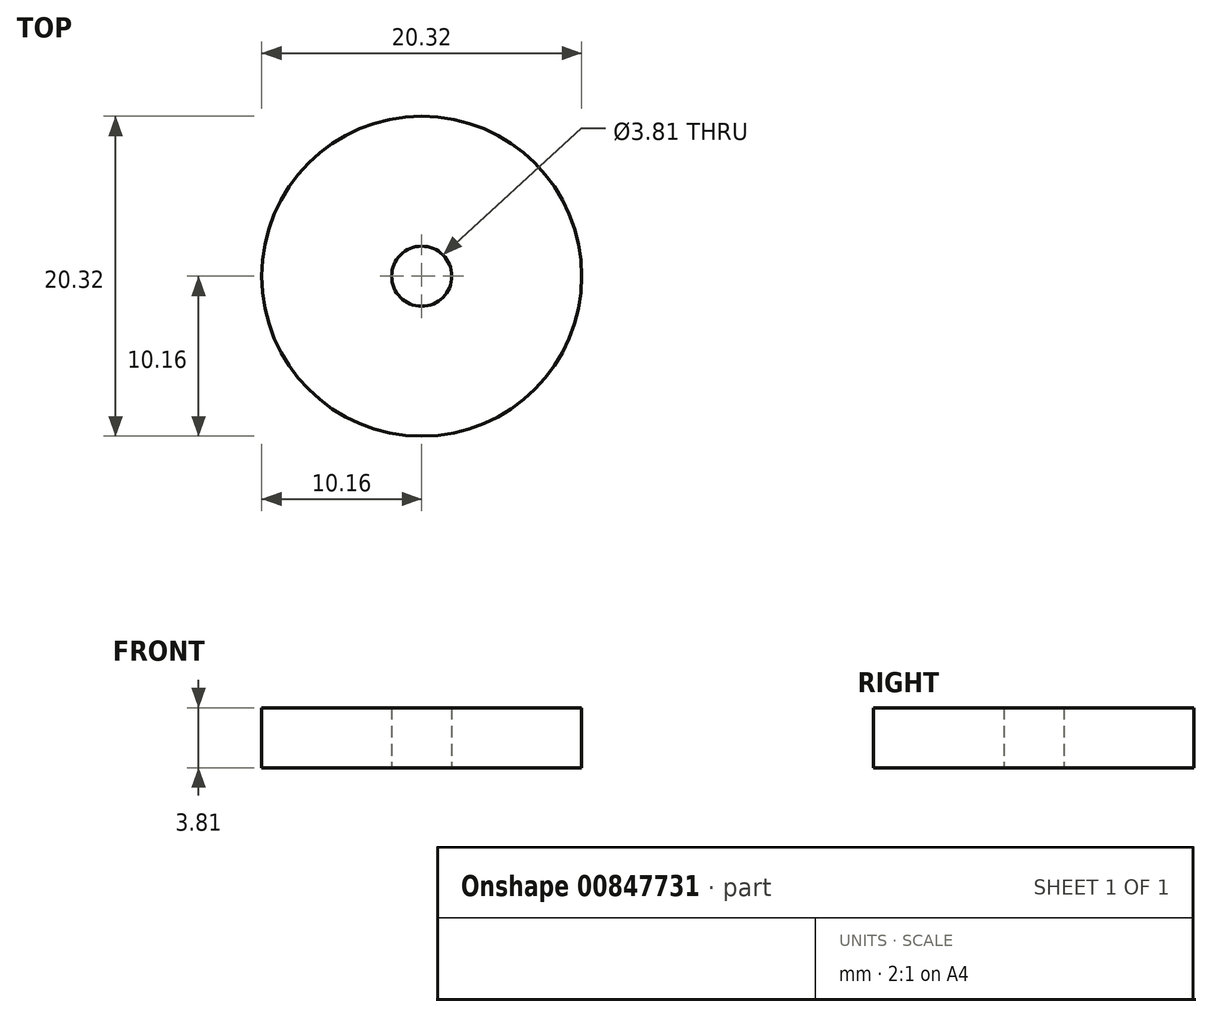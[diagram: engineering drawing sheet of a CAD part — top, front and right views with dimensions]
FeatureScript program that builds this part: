
annotation { "Feature Type Name" : "Feature", "Feature Type Description" : "" }
export const myFeature = defineFeature(function(context is Context, id is Id, definition is map)
    precondition{}
    {
        {
            var Q0;
            Q0=qCreatedBy(makeId("Top.planeOp"),FACE);
            var sketch = newSketch(context, id + "F0", { "sketchPlane" : qUnion([Q0])});
            skCircle(sketch, "E0", {"center": v(0, 0) * mm, "radius": 10.16 * mm});
            skSolve(sketch);
        }
        {
            var Q0;
            Q0=makeQuery(id+"F0.imprint","IMPRINT",FACE,{"disambiguationData":[TD([[makeQuery(id+"F0.imprint","IMPRINT",EDGE,{"derivedFrom":sQuery(id+"F0.wireOp",EDGE,"E0")}),1.0]])]});
            extrude(context, id + "F1", {"entities" : qUnion([Q0]), "depth" : 3.8 * mm, "offsetDistance" : 25.4 * mm});
        }
        {
            var Q0;
            Q0=qCreatedBy(makeId("Front.planeOp"),FACE);
            var sketch = newSketch(context, id + "F2", { "sketchPlane" : qUnion([Q0])});
            skLineSegment(sketch, "E1", {"start": v(-8.9, 3.81) * mm, "end": v(0, 3.81) * mm});
            skLineSegment(sketch, "E2", {"start": v(0, 3.81) * mm, "end": v(0, 1.78) * mm});
            skArc(sketch, "E3", {"start": v(-8.9, 3.8) * mm, "mid": v(-4.56, 2.3) * mm, "end": v(0, 1.78) * mm});
            skLineSegment(sketch, "E4", {"start": v(0, 1.78) * mm, "end": v(21.03, 1.78) * mm, "construction": true});
            skSolve(sketch);
        }
        {
            var Q0;
            Q0=makeQuery(id+"F1.opExtrude","CAP_FACE",FACE,{"disambiguationData":[OSD([sQuery(id+"F0.wireOp",EDGE,"E0")])],"isStart":true});
            var sketch = newSketch(context, id + "F3", { "sketchPlane" : qUnion([Q0])});
            skCircle(sketch, "E5", {"center": v(0, 0) * mm, "radius": 1.9 * mm});
            skSolve(sketch);
        }
        {
            var Q0;
            Q0=qSketchRegion(id+"F3",true);
            extrude(context, id + "F4", {"entities" : qUnion([Q0]), "operationType" : NewBodyOperationType.REMOVE, "oppositeDirection" : true, "depth" : 7.62 * mm, "offsetDistance" : 25.4 * mm});
        }
    });
